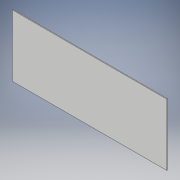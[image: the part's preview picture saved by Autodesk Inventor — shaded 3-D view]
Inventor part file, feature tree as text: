
AUTODESK INVENTOR PART (.ipt)
format: ipt  version: 2019 (Build 230136000, 136)  size: 89,600 bytes
history: native  units: mm
features: extrude x1, sketch x1
ambient origin geometry x8: Origin, YZ Plane, XZ Plane, XY Plane, X Axis, Y Axis, Z Axis, Center Point
bodies: Solid1 (feature_tree)
feature tree (2):
  extrude  "Extrusion1"  Depth=800.0mm
  sketch  "Sketch1"  dims[d0=2000.0mm d1=800.0mm d2=10.0mm d3=0.0mm]
